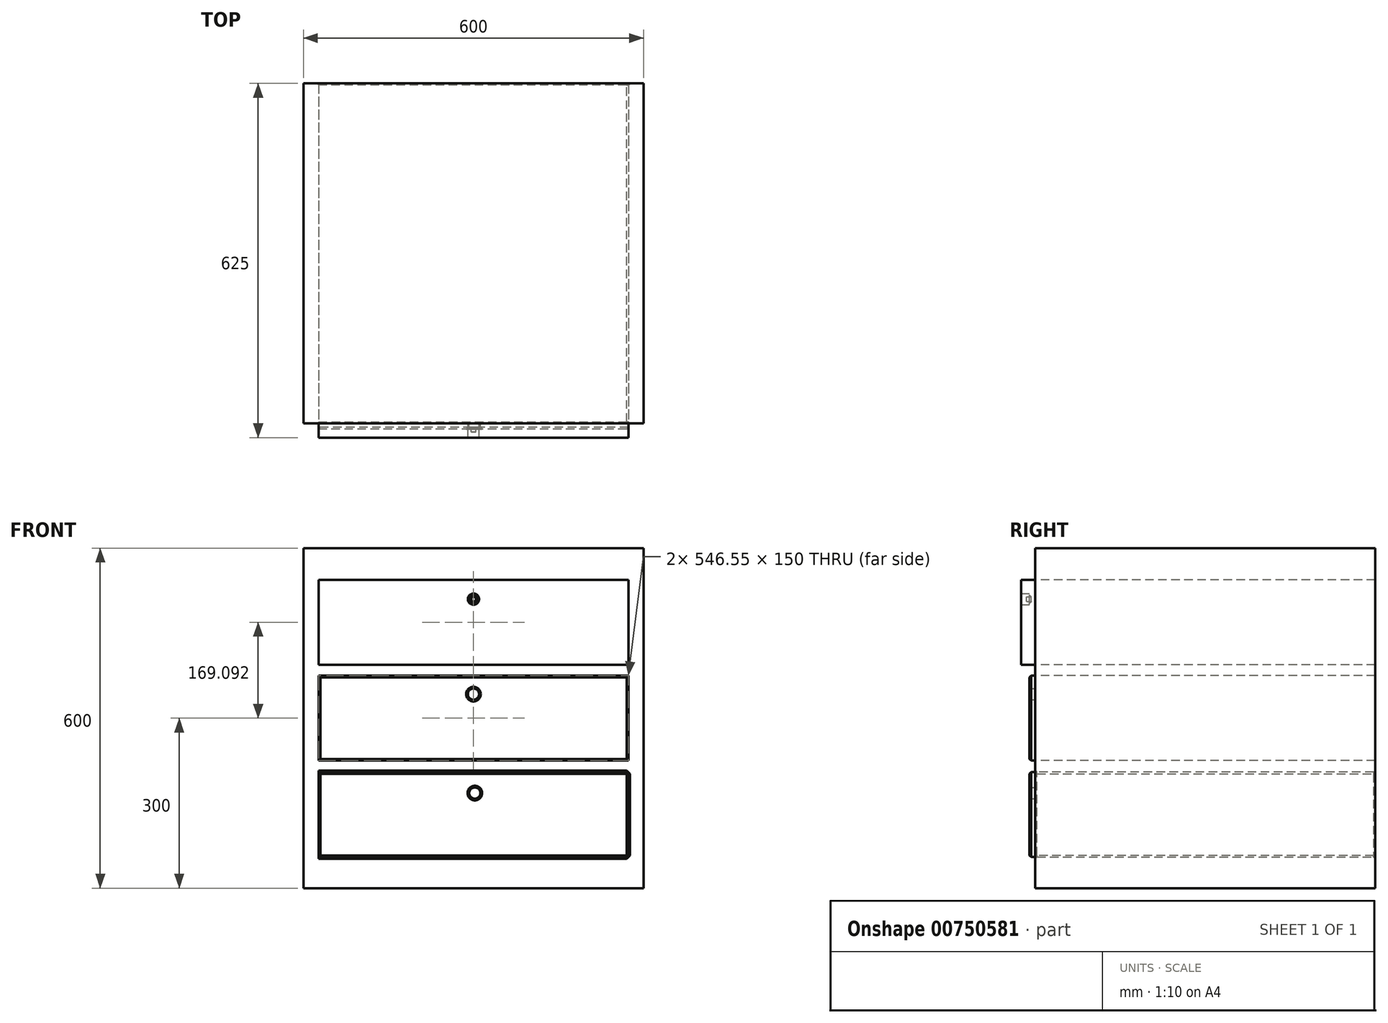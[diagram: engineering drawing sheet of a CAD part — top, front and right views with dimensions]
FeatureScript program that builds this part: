
annotation { "Feature Type Name" : "Feature", "Feature Type Description" : "" }
export const myFeature = defineFeature(function(context is Context, id is Id, definition is map)
    precondition{}
    {
        {
            var Q0;
            Q0=qCreatedBy(makeId("Front.planeOp"),FACE);
            var sketch = newSketch(context, id + "F0", { "sketchPlane" : qUnion([Q0])});
            skLineSegment(sketch, "E0.bottom", {"start": v(300, -300) * mm, "end": v(-300, -300) * mm});
            skLineSegment(sketch, "E0.top", {"start": v(300, 300) * mm, "end": v(-300, 300) * mm});
            skLineSegment(sketch, "E0.left", {"start": v(300, -300) * mm, "end": v(300, 300) * mm});
            skLineSegment(sketch, "E0.right", {"start": v(-300, -300) * mm, "end": v(-300, 300) * mm});
            skPoint(sketch, "E0.middle", {"position": v(0, 0) * mm});
            skLineSegment(sketch, "E1.bottom", {"start": v(273.28, 94.1) * mm, "end": v(-273.28, 94.1) * mm});
            skLineSegment(sketch, "E1.top", {"start": v(273.28, 244.1) * mm, "end": v(-273.28, 244.1) * mm});
            skLineSegment(sketch, "E1.left", {"start": v(273.28, 94.1) * mm, "end": v(273.28, 244.1) * mm});
            skLineSegment(sketch, "E1.right", {"start": v(-273.28, 94.1) * mm, "end": v(-273.28, 244.1) * mm});
            skPoint(sketch, "E1.middle", {"position": v(0, 169.1) * mm});
            skLineSegment(sketch, "E2.bottom", {"start": v(273.28, -75) * mm, "end": v(-273.28, -75) * mm});
            skLineSegment(sketch, "E2.top", {"start": v(273.28, 75) * mm, "end": v(-273.28, 75) * mm});
            skLineSegment(sketch, "E2.left", {"start": v(273.28, -75) * mm, "end": v(273.28, 75) * mm});
            skLineSegment(sketch, "E2.right", {"start": v(-273.28, -75) * mm, "end": v(-273.28, 75) * mm});
            skLineSegment(sketch, "E3.bottom", {"start": v(273.28, -245.3) * mm, "end": v(-273.28, -245.3) * mm});
            skLineSegment(sketch, "E3.top", {"start": v(273.28, -95.3) * mm, "end": v(-273.28, -95.3) * mm});
            skLineSegment(sketch, "E3.left", {"start": v(273.28, -245.3) * mm, "end": v(273.28, -95.3) * mm});
            skLineSegment(sketch, "E3.right", {"start": v(-273.28, -245.3) * mm, "end": v(-273.28, -95.3) * mm});
            skPoint(sketch, "E3.middle", {"position": v(0, -170.3) * mm});
            skPoint(sketch, "E4", {"position": v(0, 75) * mm});
            skCircle(sketch, "E5", {"center": v(0, 209.95) * mm, "radius": 4.22 * mm});
            skCircle(sketch, "E6", {"center": v(0, 209.95) * mm, "radius": 9.9 * mm});
            skCircle(sketch, "E7", {"center": v(0, 42.36) * mm, "radius": 4.22 * mm});
            skCircle(sketch, "E8", {"center": v(0, 42.36) * mm, "radius": 9.9 * mm});
            skCircle(sketch, "E9", {"center": v(2.4, -132.24) * mm, "radius": 4.22 * mm});
            skCircle(sketch, "E10", {"center": v(2.4, -132.24) * mm, "radius": 9.9 * mm});
            skSolve(sketch);
        }
        {
            var Q0;
            Q0=makeQuery(id+"F0.imprint","IMPRINT",FACE,{"disambiguationData":[TD([[makeQuery(id+"F0.imprint","IMPRINT",EDGE,{"derivedFrom":sQuery(id+"F0.wireOp",EDGE,"E0.bottom")}),-1.0]])]});
            extrude(context, id + "F1", {"entities" : qUnion([Q0]), "oppositeDirection" : true, "depth" : 600 * mm, "offsetDistance" : 25 * mm});
        }
        {
            var Q0;
            Q0=makeQuery(id+"F0.imprint","IMPRINT",FACE,{"disambiguationData":[TD([[makeQuery(id+"F0.imprint","IMPRINT",EDGE,{"derivedFrom":sQuery(id+"F0.wireOp",EDGE,"E1.bottom")}),-1.0]])]});
            var Q1;
            Q1=makeQuery(id+"F0.imprint","IMPRINT",FACE,{"disambiguationData":[TD([[makeQuery(id+"F0.imprint","IMPRINT",EDGE,{"derivedFrom":sQuery(id+"F0.wireOp",EDGE,"E5")}),-1.0]])]});
            extrude(context, id + "F2", {"entities" : qUnion([Q0, Q1]), "depth" : 10 * mm, "offsetDistance" : 25 * mm});
        }
        {
            var Q0;
            Q0=makeQuery(id+"F2.opExtrude","CAP_FACE",FACE,{"disambiguationData":[OSD([sQuery(id+"F0.wireOp",EDGE,"E1.bottom"),sQuery(id+"F0.wireOp",EDGE,"E1.top"),sQuery(id+"F0.wireOp",EDGE,"E1.left"),sQuery(id+"F0.wireOp",EDGE,"E1.right"),sQuery(id+"F0.wireOp",EDGE,"E6")])],"isStart":false});
            chamfer(context, id + "F3", {"entities" : qUnion([Q0]), "width" : 3 * mm, "tangentPropagation" : true});
        }
        {
            var Q0;
            Q0=makeQuery(id+"F0.imprint","IMPRINT",FACE,{"disambiguationData":[TD([[makeQuery(id+"F0.imprint","IMPRINT",EDGE,{"derivedFrom":sQuery(id+"F0.wireOp",EDGE,"E2.bottom")}),-1.0]])]});
            extrude(context, id + "F4", {"entities" : qUnion([Q0]), "depth" : 10 * mm, "offsetDistance" : 25 * mm});
        }
        {
            var Q0;
            Q0=makeQuery(id+"F4.opExtrude","CAP_FACE",FACE,{"disambiguationData":[OSD([sQuery(id+"F0.wireOp",EDGE,"E2.bottom"),sQuery(id+"F0.wireOp",EDGE,"E2.top"),sQuery(id+"F0.wireOp",EDGE,"E2.left"),sQuery(id+"F0.wireOp",EDGE,"E2.right"),sQuery(id+"F0.wireOp",EDGE,"E8")])],"isStart":false});
            var Q1;
            Q1=makeQuery(id+"F1.opExtrude","SWEPT_FACE",FACE,{"disambiguationData":[OSD([sQuery(id+"F0.wireOp",EDGE,"E3.left")])]});
            chamfer(context, id + "F5", {"entities" : qUnion([Q0, Q1]), "width" : 3 * mm, "tangentPropagation" : true});
        }
        {
            var Q0;
            Q0=makeQuery(id+"F0.imprint","IMPRINT",FACE,{"disambiguationData":[TD([[makeQuery(id+"F0.imprint","IMPRINT",EDGE,{"derivedFrom":sQuery(id+"F0.wireOp",EDGE,"E3.bottom")}),-1.0]])]});
            extrude(context, id + "F6", {"entities" : qUnion([Q0]), "depth" : 10 * mm, "offsetDistance" : 25 * mm});
        }
        {
            var Q0;
            Q0=makeQuery(id+"F6.opExtrude","CAP_FACE",FACE,{"disambiguationData":[OSD([sQuery(id+"F0.wireOp",EDGE,"E3.bottom"),sQuery(id+"F0.wireOp",EDGE,"E3.top"),sQuery(id+"F0.wireOp",EDGE,"E3.left"),sQuery(id+"F0.wireOp",EDGE,"E3.right"),sQuery(id+"F0.wireOp",EDGE,"E10")])],"isStart":false});
            chamfer(context, id + "F7", {"entities" : qUnion([Q0]), "width" : 3 * mm, "tangentPropagation" : true});
        }
        {
            var Q0;
            Q0=makeQuery(id+"F0.imprint","IMPRINT",FACE,{"disambiguationData":[TD([[makeQuery(id+"F0.imprint","IMPRINT",EDGE,{"derivedFrom":sQuery(id+"F0.wireOp",EDGE,"E5")}),1.0]])]});
            var Q1;
            Q1=sQuery(id+"F0.wireOp",EDGE,"E5");
            extrude(context, id + "F8", {"entities" : qUnion([Q0]), "operationType" : NewBodyOperationType.ADD, "surfaceOperationType" : NewSurfaceOperationType.ADD, "surfaceEntities" : qUnion([Q1]), "depth" : 15 * mm, "offsetDistance" : 25 * mm});
        }
        {
            var Q0;
            Q0=makeQuery(id+"F0.imprint","IMPRINT",FACE,{"disambiguationData":[TD([[makeQuery(id+"F0.imprint","IMPRINT",EDGE,{"derivedFrom":sQuery(id+"F0.wireOp",EDGE,"E1.bottom")}),-1.0]])]});
            var Q1;
            Q1=sQuery(id+"F0.wireOp",EDGE,"E6");
            extrude(context, id + "F9", {"entities" : qUnion([Q0]), "operationType" : NewBodyOperationType.ADD, "surfaceOperationType" : NewSurfaceOperationType.ADD, "surfaceEntities" : qUnion([Q1]), "depth" : 25 * mm, "offsetDistance" : 25 * mm});
        }
    });
